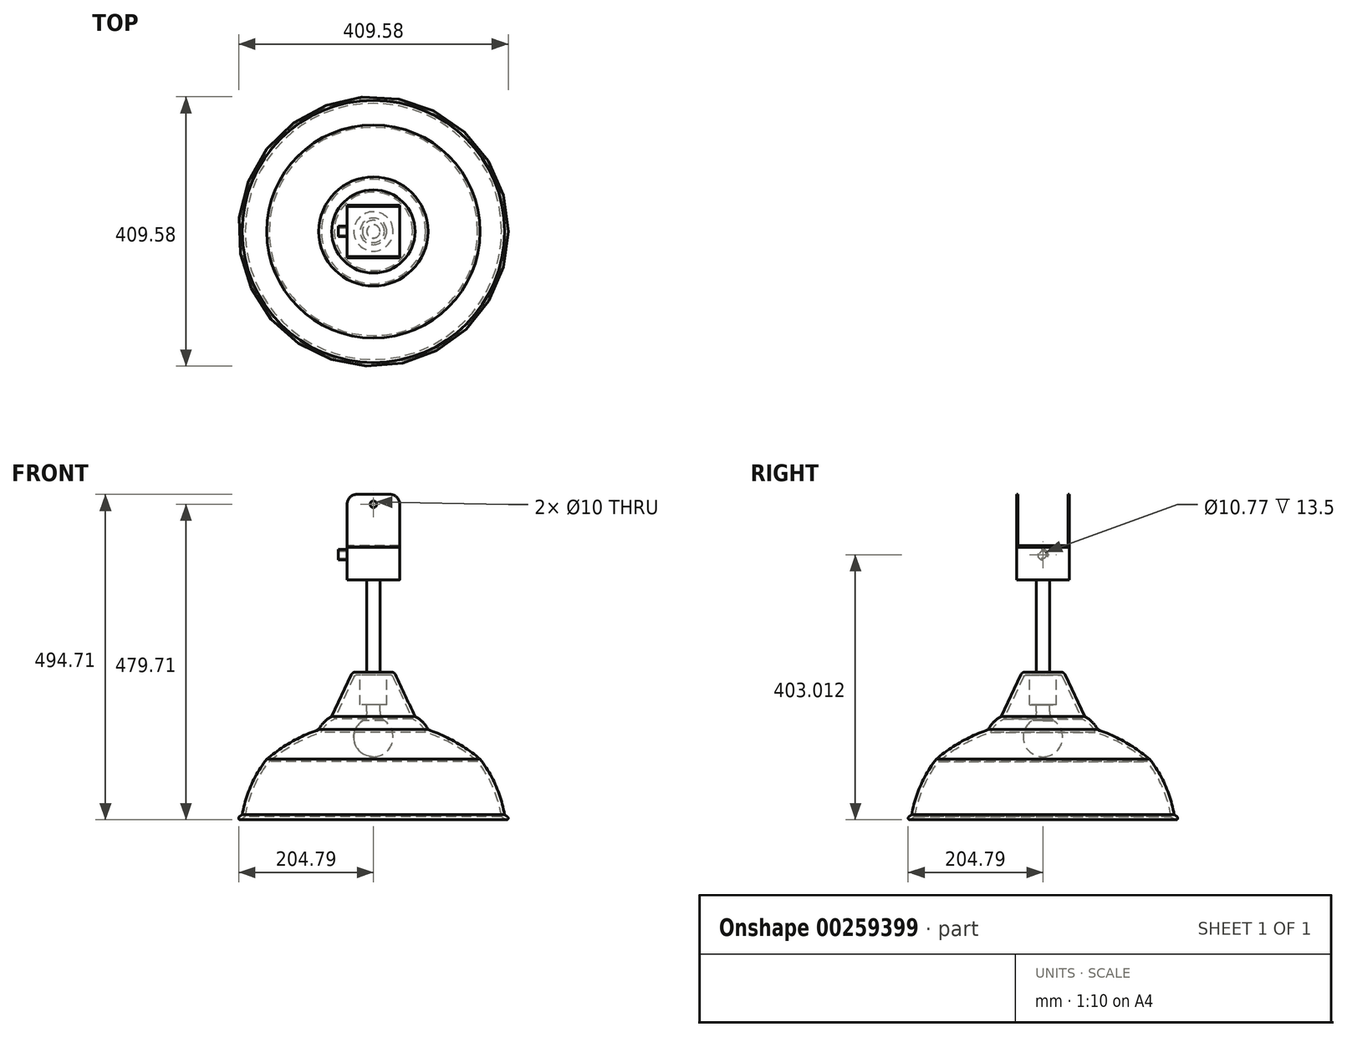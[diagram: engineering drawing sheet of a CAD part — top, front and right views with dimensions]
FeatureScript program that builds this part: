
annotation { "Feature Type Name" : "Feature", "Feature Type Description" : "" }
export const myFeature = defineFeature(function(context is Context, id is Id, definition is map)
    precondition{}
    {
        {
            var Q0;
            Q0=qCreatedBy(makeId("Front.planeOp"),FACE);
            var sketch = newSketch(context, id + "F0", { "sketchPlane" : qUnion([Q0])});
            skLineSegment(sketch, "E0", {"start": v(0, 225) * mm, "end": v(-26.93, 225) * mm});
            skLineSegment(sketch, "E1", {"start": v(-33.65, 220.72) * mm, "end": v(-63.28, 157.18) * mm});
            skLineSegment(sketch, "E2", {"start": v(-199.27, 8.03) * mm, "end": v(-203.75, 4.82) * mm});
            skArc(sketch, "E3", {"start": v(-203.75, 4.82) * mm, "mid": v(-204.33, 1.33) * mm, "end": v(-200.84, 0.75) * mm});
            skArc(sketch, "E4", {"start": v(-82.93, 137.4) * mm, "mid": v(-124.57, 118.63) * mm, "end": v(-162.01, 92.48) * mm});
            skArc(sketch, "E5", {"start": v(-63.28, 157.18) * mm, "mid": v(-74.8, 148.97) * mm, "end": v(-82.93, 137.4) * mm});
            skArc(sketch, "E6.filletArc", {"start": v(-26.93, 225) * mm, "mid": v(-30.91, 223.84) * mm, "end": v(-33.65, 220.72) * mm});
            skArc(sketch, "E7", {"start": v(-162.01, 92.48) * mm, "mid": v(-185.87, 52.56) * mm, "end": v(-199.27, 8.03) * mm});
            skLineSegment(sketch, "E8.0", {"start": v(-194.67, 5.17) * mm, "end": v(-200.84, 0.75) * mm});
            skArc(sketch, "E8.1", {"start": v(-158.39, 89) * mm, "mid": v(-181.8, 49.37) * mm, "end": v(-194.67, 5.17) * mm});
            skArc(sketch, "E8.2", {"start": v(-79.25, 133.37) * mm, "mid": v(-120.93, 114.95) * mm, "end": v(-158.39, 89) * mm});
            skLineSegment(sketch, "E8.3", {"start": v(0, 220) * mm, "end": v(-26.93, 220) * mm});
            skArc(sketch, "E8.4", {"start": v(-26.93, 220) * mm, "mid": v(-28.23, 219.62) * mm, "end": v(-29.12, 218.6) * mm});
            skLineSegment(sketch, "E8.5", {"start": v(-29.12, 218.6) * mm, "end": v(-59.53, 153.4) * mm});
            skArc(sketch, "E8.6", {"start": v(-59.53, 153.4) * mm, "mid": v(-71.37, 145.33) * mm, "end": v(-79.25, 133.37) * mm});
            skLineSegment(sketch, "E9", {"start": v(-200.84, 0.75) * mm, "end": v(-200.84, 0.75) * mm});
            skLineSegment(sketch, "E10", {"start": v(0, 225) * mm, "end": v(0, 220) * mm});
            skLineSegment(sketch, "E11.bottom", {"start": v(0, 220) * mm, "end": v(-20.24, 220) * mm});
            skLineSegment(sketch, "E11.top", {"start": v(0, 175) * mm, "end": v(-20.24, 175) * mm});
            skLineSegment(sketch, "E11.left", {"start": v(0, 220) * mm, "end": v(0, 175) * mm});
            skLineSegment(sketch, "E11.right", {"start": v(-20.24, 220) * mm, "end": v(-20.24, 175) * mm});
            skPoint(sketch, "E12.oppositeSnap0", {"position": v(-10.12, 175) * mm});
            skLineSegment(sketch, "E12.bottom", {"start": v(0, 175) * mm, "end": v(-10.12, 175) * mm});
            skLineSegment(sketch, "E12.top", {"start": v(0, 165) * mm, "end": v(-10.12, 165) * mm});
            skLineSegment(sketch, "E12.left", {"start": v(0, 175) * mm, "end": v(0, 165) * mm});
            skLineSegment(sketch, "E12.right", {"start": v(-10.12, 175) * mm, "end": v(-10.12, 165) * mm});
            skArc(sketch, "E13", {"start": v(0, 155.96) * mm, "mid": v(-29.96, 126) * mm, "end": v(0, 96.04) * mm});
            skArc(sketch, "E14", {"start": v(-10.12, 165) * mm, "mid": v(-11.88, 157.13) * mm, "end": v(-16.84, 150.78) * mm});
            skLineSegment(sketch, "E15", {"start": v(0, 165) * mm, "end": v(0, 155.96) * mm});
            skLineSegment(sketch, "E16", {"start": v(0, 155.96) * mm, "end": v(0, 155.96) * mm});
            skLineSegment(sketch, "E17", {"start": v(0, 155.96) * mm, "end": v(0, 126) * mm});
            skLineSegment(sketch, "E18", {"start": v(0, 126) * mm, "end": v(0, 96.04) * mm});
            skLineSegment(sketch, "E19.bottom", {"start": v(0, 225) * mm, "end": v(-10, 225) * mm});
            skLineSegment(sketch, "E19.top", {"start": v(0, 365) * mm, "end": v(-10, 365) * mm});
            skLineSegment(sketch, "E19.left", {"start": v(0, 225) * mm, "end": v(0, 365) * mm});
            skLineSegment(sketch, "E19.right", {"start": v(-10, 225) * mm, "end": v(-10, 365) * mm});
            skSolve(sketch);
        }
        {
            var Q0;
            Q0 = qSketchRegion(id + "F0", true);
            var Q1;
            Q1 = qConstructionFilter(qBodyType(qCreatedBy(id + "F0" ,EDGE), BodyType.WIRE), ConstructionObject.NO);
            var Q2;
            Q2=sQuery(id+"F0.wireOp",EDGE,"E10");
            revolve(context, id + "F1", {"entities" : qUnion([Q0]), "surfaceEntities" : qUnion([Q1]), "axis" : qUnion([Q2]), "revolveType" : RevolveType.FULL});
        }
        {
            var Q0;
            Q0=makeQuery(id+"F1.opRevolve","SWEPT_FACE",FACE,{"disambiguationData":[OSD([sQuery(id+"F0.wireOp",EDGE,"E19.top")])]});
            var sketch = newSketch(context, id + "F2", { "sketchPlane" : qUnion([Q0])});
            skLineSegment(sketch, "E20.bottom", {"start": v(35, 40) * mm, "end": v(-35, 40) * mm});
            skLineSegment(sketch, "E20.top", {"start": v(35, -40) * mm, "end": v(-35, -40) * mm});
            skLineSegment(sketch, "E20.left", {"start": v(40, 35) * mm, "end": v(40, -35) * mm});
            skLineSegment(sketch, "E20.right", {"start": v(-40, 35) * mm, "end": v(-40, -35) * mm});
            skPoint(sketch, "E20.middle", {"position": v(0, 0) * mm});
            skPoint(sketch, "E21.visualSharp", {"position": v(-40, 40) * mm});
            skArc(sketch, "E21.filletArc", {"start": v(-35, 40) * mm, "mid": v(-38.54, 38.54) * mm, "end": v(-40, 35) * mm});
            skPoint(sketch, "E22.visualSharp", {"position": v(40, 40) * mm});
            skArc(sketch, "E22.filletArc", {"start": v(40, 35) * mm, "mid": v(38.54, 38.54) * mm, "end": v(35, 40) * mm});
            skPoint(sketch, "E23.visualSharp", {"position": v(40, -40) * mm});
            skArc(sketch, "E23.filletArc", {"start": v(35, -40) * mm, "mid": v(38.54, -38.54) * mm, "end": v(40, -35) * mm});
            skPoint(sketch, "E24.visualSharp", {"position": v(-40, -40) * mm});
            skArc(sketch, "E24.filletArc", {"start": v(-40, -35) * mm, "mid": v(-38.54, -38.54) * mm, "end": v(-35, -40) * mm});
            skSolve(sketch);
        }
        {
            var Q0;
            Q0 = qSketchRegion(id + "F2", true);
            extrude(context, id + "F3", {"entities" : qUnion([Q0]), "operationType" : NewBodyOperationType.ADD, "depth" : 50 * mm});
        }
        {
            var Q0;
            Q0=makeQuery(id+"F3.opExtrude","SWEPT_FACE",FACE,{"disambiguationData":[OSD([sQuery(id+"F2.wireOp",EDGE,"E20.right")])]});
            var sketch = newSketch(context, id + "F4", { "sketchPlane" : qUnion([Q0])});
            skCircle(sketch, "E25", {"center": v(0, 403.3) * mm, "radius": 7.86 * mm});
            skCircle(sketch, "E26", {"center": v(0, 403.3) * mm, "radius": 5.39 * mm});
            skSolve(sketch);
        }
        {
            var Q0;
            Q0=makeQuery(id+"F4.imprint","IMPRINT",FACE,{"disambiguationData":[TD([[makeQuery(id+"F4.imprint","IMPRINT",EDGE,{"derivedFrom":sQuery(id+"F4.wireOp",EDGE,"E25")}),1.0]])]});
            extrude(context, id + "F5", {"entities" : qUnion([Q0]), "operationType" : NewBodyOperationType.ADD, "depth" : 13.5 * mm});
        }
        {
            var Q0;
            {var subQ0=sQuery(id+"F2.wireOp",EDGE,"E21.filletArc");var subQ4=sQuery(id+"F2.wireOp",EDGE,"E20.right");Q0=makeQuery(id+"F5.boolean.opBoolean","SPLIT",FACE,{"disambiguationData":[TD([makeQuery(id+"F3.opExtrude","SWEPT_FACE",FACE,{"disambiguationData":[OSD([subQ0])]})])],"derivedFrom":makeQuery(id+"F3.opExtrude","SWEPT_FACE",FACE,{"disambiguationData":[OSD([subQ4])]})});}
            var sketch = newSketch(context, id + "F6", { "sketchPlane" : qUnion([Q0])});
            skLineSegment(sketch, "E27.bottom", {"start": v(40, 495) * mm, "end": v(38, 495) * mm});
            skLineSegment(sketch, "E27.top", {"start": v(40, 415) * mm, "end": v(-40, 415) * mm});
            skLineSegment(sketch, "E27.left", {"start": v(40, 495) * mm, "end": v(40, 415) * mm});
            skLineSegment(sketch, "E27.right", {"start": v(-40, 495) * mm, "end": v(-40, 415) * mm});
            skPoint(sketch, "E27.middle", {"position": v(0, 455) * mm});
            skLineSegment(sketch, "E28.0", {"start": v(38, 495) * mm, "end": v(38, 417) * mm});
            skLineSegment(sketch, "E28.1", {"start": v(38, 417) * mm, "end": v(-38, 417) * mm});
            skLineSegment(sketch, "E28.2", {"start": v(-38, 495) * mm, "end": v(-38, 417) * mm});
            skLineSegment(sketch, "E29.trimOffspring", {"start": v(-38, 495) * mm, "end": v(-40, 495) * mm});
            skSolve(sketch);
        }
        {
            var Q0;
            Q0 = qSketchRegion(id + "F6", true);
            var Q1;
            Q1=makeQuery(id+"F3.opExtrude","SWEPT_FACE",FACE,{"disambiguationData":[OSD([sQuery(id+"F2.wireOp",EDGE,"E20.left")])]});
            extrude(context, id + "F7", {"entities" : qUnion([Q0]), "operationType" : NewBodyOperationType.ADD, "endBound" : BoundingType.UP_TO_SURFACE, "oppositeDirection" : true, "endBoundEntityFace" : qUnion([Q1]), "depth" : 25 * mm});
        }
        {
            var Q0;
            Q0=makeQuery(id+"F7.opExtrude","CAP_EDGE",EDGE,{"disambiguationData":[OSD([sQuery(id+"F6.wireOp",EDGE,"E29.trimOffspring")])],"isStart":false});
            var Q1;
            Q1=makeQuery(id+"F7.opExtrude","CAP_EDGE",EDGE,{"disambiguationData":[OSD([sQuery(id+"F6.wireOp",EDGE,"E27.bottom")])],"isStart":false});
            var Q2;
            Q2=makeQuery(id+"F7.opExtrude","CAP_EDGE",EDGE,{"disambiguationData":[OSD([sQuery(id+"F6.wireOp",EDGE,"E29.trimOffspring")])],"isStart":true});
            var Q3;
            Q3=makeQuery(id+"F7.opExtrude","CAP_EDGE",EDGE,{"disambiguationData":[OSD([sQuery(id+"F6.wireOp",EDGE,"E27.bottom")])],"isStart":true});
            fillet(context, id + "F8", {"entities" : qUnion([Q0, Q1, Q2, Q3]), "radius" : 15 * mm, "allowEdgeOverflow" : false});
        }
        {
            var Q0;
            Q0=makeQuery(id+"F7.boolean.opBoolean","MERGE",FACE,{"derivedFrom":[makeQuery(id+"F3.opExtrude","SWEPT_FACE",FACE,{"disambiguationData":[OSD([sQuery(id+"F2.wireOp",EDGE,"E20.bottom")])]}),makeQuery(id+"F7.opExtrude","SWEPT_FACE",FACE,{"disambiguationData":[OSD([sQuery(id+"F6.wireOp",EDGE,"E27.right")])]})]});
            var sketch = newSketch(context, id + "F9", { "sketchPlane" : qUnion([Q0])});
            skCircle(sketch, "E30", {"center": v(0, 480) * mm, "radius": 5 * mm});
            skSolve(sketch);
        }
        {
            var Q0;
            Q0 = qSketchRegion(id + "F9", true);
            extrude(context, id + "F10", {"entities" : qUnion([Q0]), "operationType" : NewBodyOperationType.REMOVE, "endBound" : BoundingType.THROUGH_ALL, "oppositeDirection" : true, "depth" : 25 * mm});
        }
        {
            var Q0;
            Q0=makeQuery(id+"F7.boolean.opBoolean","MERGE",FACE,{"derivedFrom":[makeQuery(id+"F3.opExtrude","SWEPT_FACE",FACE,{"disambiguationData":[OSD([sQuery(id+"F2.wireOp",EDGE,"E20.bottom")])]}),makeQuery(id+"F7.opExtrude","SWEPT_FACE",FACE,{"disambiguationData":[OSD([sQuery(id+"F6.wireOp",EDGE,"E27.right")])]})]});
            var sketch = newSketch(context, id + "F11", { "sketchPlane" : qUnion([Q0])});
            skLineSegment(sketch, "E31.bottom", {"start": v(-40, 415) * mm, "end": v(40, 415) * mm});
            skLineSegment(sketch, "E31.top", {"start": v(-40, 414.5) * mm, "end": v(40, 414.5) * mm});
            skLineSegment(sketch, "E31.left", {"start": v(-40, 415) * mm, "end": v(-40, 414.5) * mm});
            skLineSegment(sketch, "E31.right", {"start": v(40, 415) * mm, "end": v(40, 414.5) * mm});
            skSolve(sketch);
        }
        {
            var Q0;
            Q0 = qSketchRegion(id + "F11", true);
            extrude(context, id + "F12", {"entities" : qUnion([Q0]), "operationType" : NewBodyOperationType.REMOVE, "endBound" : BoundingType.THROUGH_ALL, "oppositeDirection" : true, "depth" : 25 * mm});
        }
    });
